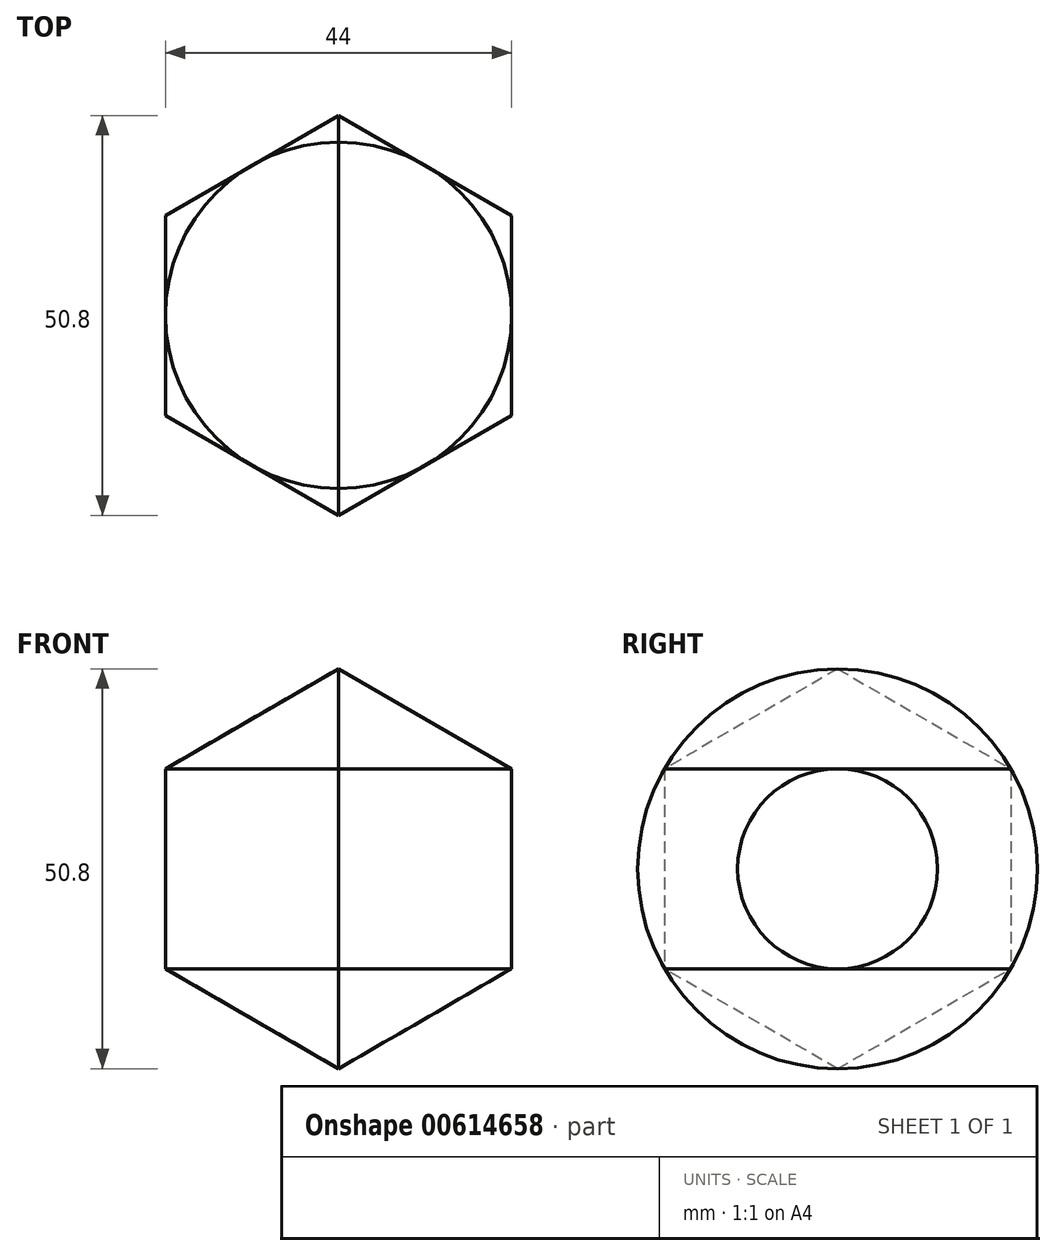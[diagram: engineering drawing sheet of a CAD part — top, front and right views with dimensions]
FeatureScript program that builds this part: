
annotation { "Feature Type Name" : "Feature", "Feature Type Description" : "" }
export const myFeature = defineFeature(function(context is Context, id is Id, definition is map)
    precondition{}
    {
        {
            var Q0;
            Q0=qCreatedBy(makeId("Front.planeOp"),FACE);
            var sketch = newSketch(context, id + "F0", { "sketchPlane" : qUnion([Q0])});
            skCircle(sketch, "E0", {"center": v(0, 0) * mm, "radius": 25.4 * mm});
            skLineSegment(sketch, "E1", {"start": v(0, 0) * mm, "end": v(0, 25.4) * mm});
            skLineSegment(sketch, "E2", {"start": v(0, 0) * mm, "end": v(0, -25.4) * mm});
            skLineSegment(sketch, "E3", {"start": v(0, 0) * mm, "end": v(-22, 12.7) * mm});
            skLineSegment(sketch, "E4", {"start": v(-22, 12.7) * mm, "end": v(-22, -12.7) * mm});
            skLineSegment(sketch, "E5", {"start": v(-22, -12.7) * mm, "end": v(0, 0) * mm});
            skLineSegment(sketch, "E6", {"start": v(-22, 12.7) * mm, "end": v(0, 25.4) * mm});
            skLineSegment(sketch, "E7", {"start": v(-22, -12.7) * mm, "end": v(0, -25.4) * mm});
            skLineSegment(sketch, "E8", {"start": v(0, 0) * mm, "end": v(22, -12.7) * mm});
            skLineSegment(sketch, "E9", {"start": v(0, 0) * mm, "end": v(22, 12.7) * mm});
            skLineSegment(sketch, "E10", {"start": v(0, 25.4) * mm, "end": v(22, 12.7) * mm});
            skLineSegment(sketch, "E11", {"start": v(22, -12.7) * mm, "end": v(22, 12.7) * mm});
            skLineSegment(sketch, "E12", {"start": v(22, -12.7) * mm, "end": v(0, -25.4) * mm});
            skLineSegment(sketch, "E13", {"start": v(0, 0) * mm, "end": v(-22, 0) * mm});
            skLineSegment(sketch, "E14", {"start": v(0, 0) * mm, "end": v(22, 0) * mm});
            skSolve(sketch);
        }
        {
            var Q0;
            Q0=makeQuery(id+"F0.imprint","IMPRINT",FACE,{"disambiguationData":[TD([[makeQuery(id+"F0.imprint","IMPRINT",EDGE,{"derivedFrom":sQuery(id+"F0.wireOp",EDGE,"E1")}),1.0]])]});
            var Q1;
            Q1=makeQuery(id+"F0.imprint","IMPRINT",FACE,{"disambiguationData":[TD([[makeQuery(id+"F0.imprint","IMPRINT",EDGE,{"derivedFrom":sQuery(id+"F0.wireOp",EDGE,"E3")}),1.0]])]});
            var Q2;
            Q2=makeQuery(id+"F0.imprint","IMPRINT",FACE,{"disambiguationData":[TD([[makeQuery(id+"F0.imprint","IMPRINT",EDGE,{"derivedFrom":sQuery(id+"F0.wireOp",EDGE,"E2")}),-1.0]])]});
            var Q3;
            {var subQ0=sQuery(id+"F0.wireOp",EDGE,"E5");Q3=makeQuery(id+"F0.imprint","IMPRINT",FACE,{"disambiguationData":[TD([[makeQuery(id+"F0.imprint","IMPRINT",EDGE,{"derivedFrom":subQ0}),1.0]])]});}
            var Q4;
            Q4=sQuery(id+"F0.wireOp",EDGE,"E1");
            revolve(context, id + "F1", {"entities" : qUnion([Q0, Q1, Q2, Q3]), "axis" : qUnion([Q4]), "revolveType" : RevolveType.FULL});
        }
        {
            var Q0;
            Q0=makeQuery(id+"F0.imprint","IMPRINT",FACE,{"disambiguationData":[TD([[makeQuery(id+"F0.imprint","IMPRINT",EDGE,{"derivedFrom":sQuery(id+"F0.wireOp",EDGE,"E2")}),-1.0]])]});
            var Q1;
            {var subQ0=sQuery(id+"F0.wireOp",EDGE,"E5");Q1=makeQuery(id+"F0.imprint","IMPRINT",FACE,{"disambiguationData":[TD([[makeQuery(id+"F0.imprint","IMPRINT",EDGE,{"derivedFrom":subQ0}),1.0]])]});}
            var Q2;
            Q2=makeQuery(id+"F0.imprint","IMPRINT",FACE,{"disambiguationData":[TD([[makeQuery(id+"F0.imprint","IMPRINT",EDGE,{"derivedFrom":sQuery(id+"F0.wireOp",EDGE,"E2")}),1.0]])]});
            var Q3;
            {var subQ0=sQuery(id+"F0.wireOp",EDGE,"E8");Q3=makeQuery(id+"F0.imprint","IMPRINT",FACE,{"disambiguationData":[TD([[makeQuery(id+"F0.imprint","IMPRINT",EDGE,{"derivedFrom":subQ0}),1.0]])]});}
            var Q4;
            Q4=sQuery(id+"F0.wireOp",EDGE,"E13");
            revolve(context, id + "F2", {"entities" : qUnion([Q0, Q1, Q2, Q3]), "axis" : qUnion([Q4]), "revolveType" : RevolveType.FULL});
        }
    });
